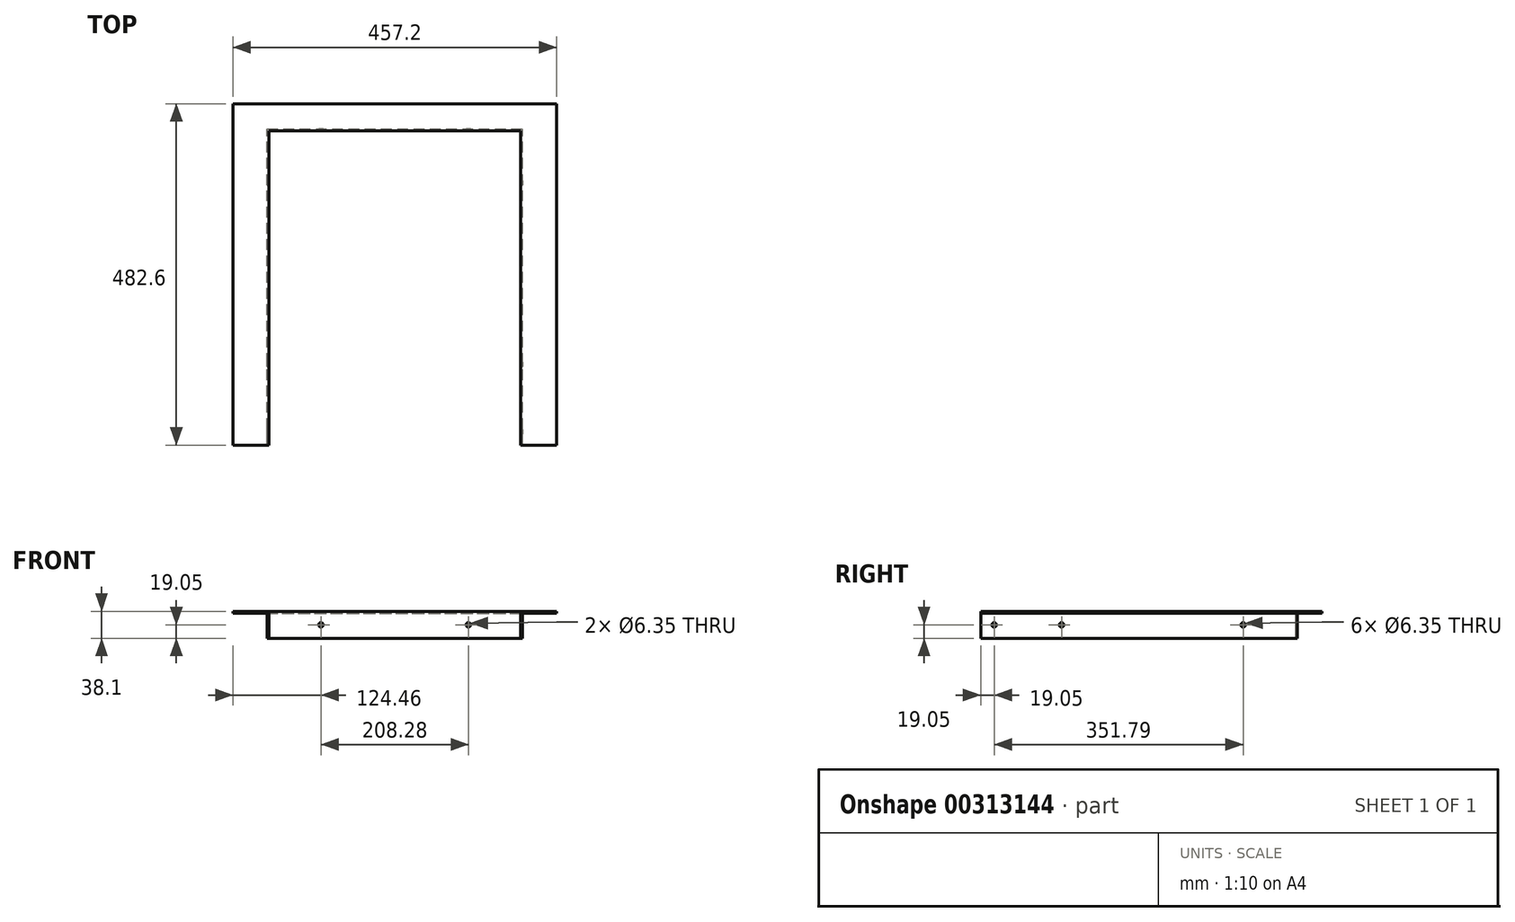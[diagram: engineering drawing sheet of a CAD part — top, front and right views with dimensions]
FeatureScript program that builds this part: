
annotation { "Feature Type Name" : "Feature", "Feature Type Description" : "" }
export const myFeature = defineFeature(function(context is Context, id is Id, definition is map)
    precondition{}
    {
        {
            var Q0;
            Q0=qCreatedBy(makeId("Top.planeOp"),FACE);
            var sketch = newSketch(context, id + "F0", { "sketchPlane" : qUnion([Q0])});
            skLineSegment(sketch, "E0.top", {"start": v(-177.8, 203.2) * mm, "end": v(177.8, 203.2) * mm});
            skLineSegment(sketch, "E0.left", {"start": v(-177.8, -241.3) * mm, "end": v(-177.8, 203.2) * mm});
            skLineSegment(sketch, "E0.right", {"start": v(177.8, -241.3) * mm, "end": v(177.8, 203.2) * mm});
            skPoint(sketch, "E0.middle", {"position": v(0, 0) * mm});
            skLineSegment(sketch, "E1.bottom", {"start": v(-228.6, 241.3) * mm, "end": v(228.6, 241.3) * mm});
            skLineSegment(sketch, "E1.top", {"start": v(-228.6, -241.3) * mm, "end": v(-177.8, -241.3) * mm});
            skLineSegment(sketch, "E1.left", {"start": v(-228.6, 241.3) * mm, "end": v(-228.6, -241.3) * mm});
            skLineSegment(sketch, "E1.right", {"start": v(228.6, 241.3) * mm, "end": v(228.6, -241.3) * mm});
            skLineSegment(sketch, "E2.trimOffspring", {"start": v(177.8, -241.3) * mm, "end": v(228.6, -241.3) * mm});
            skPoint(sketch, "E3", {"position": v(0, 241.3) * mm});
            skSolve(sketch);
        }
        {
            var Q0;
            Q0 = qSketchRegion(id + "F0", true);
            extrude(context, id + "F1", {"entities" : qUnion([Q0]), "depth" : 38.1 * mm});
        }
        {
            var Q0;
            Q0=makeQuery(id+"F1.opExtrude","CAP_FACE",FACE,{"disambiguationData":[OSD([sQuery(id+"F0.wireOp",EDGE,"E0.top"),sQuery(id+"F0.wireOp",EDGE,"E0.left"),sQuery(id+"F0.wireOp",EDGE,"E0.right"),sQuery(id+"F0.wireOp",EDGE,"E1.bottom"),sQuery(id+"F0.wireOp",EDGE,"E1.top"),sQuery(id+"F0.wireOp",EDGE,"E1.left"),sQuery(id+"F0.wireOp",EDGE,"E1.right"),sQuery(id+"F0.wireOp",EDGE,"E2.trimOffspring")])],"isStart":true});
            var Q1;
            Q1=makeQuery(id+"F1.opExtrude","SWEPT_FACE",FACE,{"disambiguationData":[OSD([sQuery(id+"F0.wireOp",EDGE,"E1.left")])]});
            var Q2;
            Q2=makeQuery(id+"F1.opExtrude","SWEPT_FACE",FACE,{"disambiguationData":[OSD([sQuery(id+"F0.wireOp",EDGE,"E1.bottom")])]});
            var Q3;
            Q3=makeQuery(id+"F1.opExtrude","SWEPT_FACE",FACE,{"disambiguationData":[OSD([sQuery(id+"F0.wireOp",EDGE,"E1.right")])]});
            var Q4;
            Q4=makeQuery(id+"F1.opExtrude","SWEPT_FACE",FACE,{"disambiguationData":[OSD([sQuery(id+"F0.wireOp",EDGE,"E2.trimOffspring")])]});
            var Q5;
            Q5=makeQuery(id+"F1.opExtrude","SWEPT_FACE",FACE,{"disambiguationData":[OSD([sQuery(id+"F0.wireOp",EDGE,"E1.top")])]});
            shell(context, id + "F2", {"entities" : qUnion([Q0, Q1, Q2, Q3, Q4, Q5]), "thickness" : 2.54 * mm});
        }
        {
            var Q0;
            Q0=makeQuery(id+"F2.opShell","OFFSET_FACE",FACE,{"disambiguationData":[OSD([sQuery(id+"F0.wireOp",EDGE,"E0.right")])]});
            var sketch = newSketch(context, id + "F3", { "sketchPlane" : qUnion([Q0])});
            skCircle(sketch, "E4", {"center": v(-222.25, 19.05) * mm, "radius": 3.18 * mm});
            skCircle(sketch, "E5", {"center": v(-127, 19.05) * mm, "radius": 3.18 * mm});
            skCircle(sketch, "E6", {"center": v(129.54, 19.05) * mm, "radius": 3.18 * mm});
            skSolve(sketch);
        }
        {
            var Q0;
            Q0 = qSketchRegion(id + "F3", true);
            extrude(context, id + "F4", {"entities" : qUnion([Q0]), "operationType" : NewBodyOperationType.REMOVE, "endBound" : BoundingType.THROUGH_ALL, "oppositeDirection" : true, "depth" : 25.4 * mm});
        }
        {
            var Q0;
            Q0=makeQuery(id+"F2.opShell","OFFSET_FACE",FACE,{"disambiguationData":[OSD([sQuery(id+"F0.wireOp",EDGE,"E0.top")])]});
            var sketch = newSketch(context, id + "F5", { "sketchPlane" : qUnion([Q0])});
            skCircle(sketch, "E7", {"center": v(-104.14, 19.05) * mm, "radius": 3.18 * mm});
            skCircle(sketch, "E8", {"center": v(104.14, 19.05) * mm, "radius": 3.18 * mm});
            skSolve(sketch);
        }
        {
            var Q0;
            Q0 = qSketchRegion(id + "F5", true);
            extrude(context, id + "F6", {"entities" : qUnion([Q0]), "operationType" : NewBodyOperationType.REMOVE, "endBound" : BoundingType.THROUGH_ALL, "oppositeDirection" : true, "depth" : 25.4 * mm});
        }
    });
